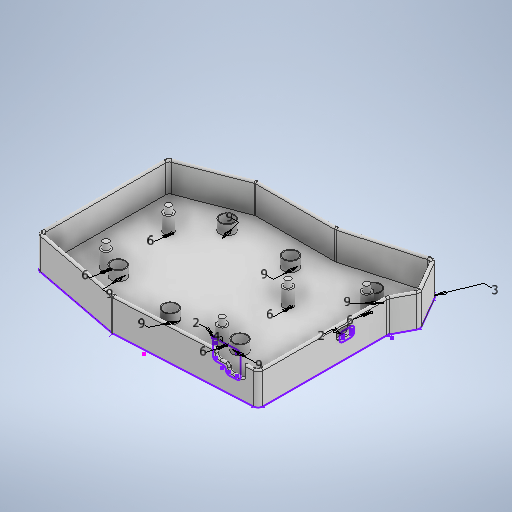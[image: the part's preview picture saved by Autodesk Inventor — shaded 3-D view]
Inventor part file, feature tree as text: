
AUTODESK INVENTOR PART (.ipt)
format: ipt  version: 2025 (Build 290162000, 162)  size: 532,480 bytes
history: native  units: mm
features: extrude x10, sketch x5, other x3, fillet x1
ambient origin geometry x8: Origin, YZ Plane, XZ Plane, XY Plane, X Axis, Y Axis, Z Axis, Center Point
bodies: Body1 (feature_tree)
feature tree (19):
  other  "Твердое тело1"
  sketch  "Эскиз1"
  sketch  "Эскиз2"
  sketch  "Эскиз3"
  extrude  "Выдавливание3"  Depth=6.0mm
  extrude  "Выдавливание4"  Depth=6.0mm
  other  "РабПлоскость4"
  sketch  "Эскиз6"
  extrude  "Выдавливание8"  Depth=6.0mm
  other  "РабПлоскость1"
  sketch  "Эскиз7"
  extrude  "Выдавливание9"  Depth=6.0mm
  extrude  "Выдавливание10"  Depth=6.0mm
  extrude  "Выдавливание11"  Depth=12.0mm TaperAngle=0.0deg
  extrude  "Выдавливание12"  Depth=16.0mm TaperAngle=0.0deg
  extrude  "Выдавливание13"  Depth=4.0mm
  extrude  "Выдавливание14"  Depth=2.0mm
  extrude  "Выдавливание15"  Depth=24.0mm TaperAngle=0.0deg
  fillet  "Сопряжение5"  Radius=24.0mm
